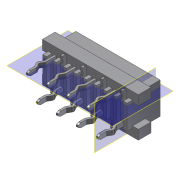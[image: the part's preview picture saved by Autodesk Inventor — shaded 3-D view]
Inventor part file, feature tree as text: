
AUTODESK INVENTOR PART (.ipt)
format: ipt  version: 2014 (Build 180170000, 170)  size: 1,097,216 bytes
history: native  units: mm
features: other x3, plane x2
ambient origin geometry x8: Origin, YZ Plane, XZ Plane, XY Plane, X Axis, Y Axis, Z Axis, Center Point
bodies: Volumenkörper1 (feature_tree)
feature tree (5):
  other  "micro-miniature_steckverbinder_a-32-08v-130x0"
  other  "Arbeitspunkt1"
  plane  "Arbeitsebene2"
  other  "Arbeitspunkt3"
  plane  "Arbeitsebene3"
